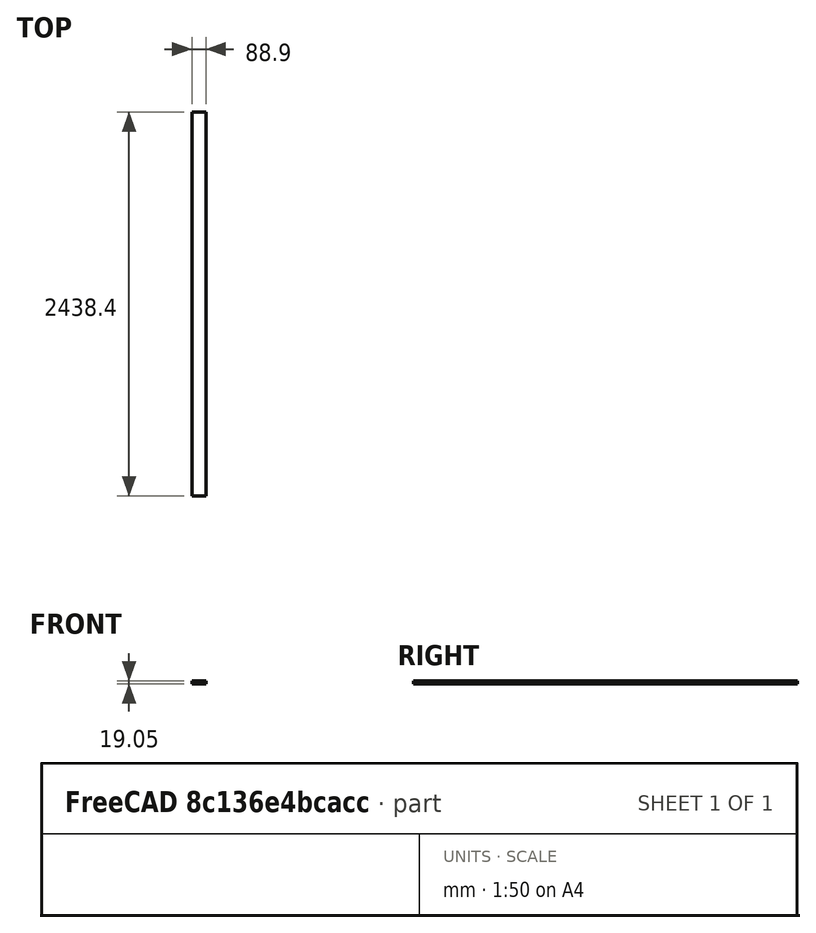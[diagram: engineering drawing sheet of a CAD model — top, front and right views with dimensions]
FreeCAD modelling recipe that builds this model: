
FCSTD DOCUMENT  (FreeCAD 0.18.3R)
Label: wood1x4
License: All rights reserved
LicenseURL: http://en.wikipedia.org/wiki/All_rights_reserved
objects: Sketcher::SketchObject×1, PartDesign::Pad×1, PartDesign::Body×1
note: 4 computed .brp shape members not serialized (recipe doc carries the construction recipe); baked Part::Feature solids carry a one-line shape summary decoded from their .brp

FEATURE [Sketcher::SketchObject] Sketch
  MapMode = 5
  Placement = pos=(0,0,0) rot=(1,0,0;1.5708rad)
  Support = -> [XZ_Plane]
  sketch-geometry (4):
    g0: LineSegment StartX=0 StartY=0 StartZ=0 EndX=-88.9 EndY=0 EndZ=0
    g1: LineSegment StartX=-88.9 StartY=0 StartZ=0 EndX=-88.9 EndY=19.05 EndZ=0
    g2: LineSegment StartX=-88.9 StartY=19.05 StartZ=0 EndX=0 EndY=19.05 EndZ=0
    g3: LineSegment StartX=0 StartY=19.05 StartZ=0 EndX=0 EndY=0 EndZ=0
  constraints (11):
    c: Coincident(g0,g1)
    c: Coincident(g1,g2)
    c: Coincident(g2,g3)
    c: Coincident(g3,g0)
    c: Horizontal(g0)
    c: Horizontal(g2)
    c: Vertical(g1)
    c: Vertical(g3)
    c: Coincident(g0,g-1)
    c: DistanceY(g3,g3) = 19.05
    c: DistanceX(g0,g0) = 88.9
FEATURE [PartDesign::Pad] Pad
  Length = 2438.4
  Length2 = 98.425
  Placement = pos=(0,0,0) rot=(1,0,0;1.5708rad)
  Profile = -> Sketch
  Type = 0
FEATURE [PartDesign::Body] Body
  Group = -> [Sketch,Pad]
  Origin = -> Origin
  Tip = -> Pad
